FREECAD ASSEMBLY — COMPONENT RECIPES ("MotorFinAssembly")

This assembly document has 18 components, labeled P0..P17 below (a component is one placed body or linked part). 8 of them carry a construction recipe — the FreeCAD feature program that regenerates the part from scratch, quoted from this document or its linked companion documents; the rest are supplied as boundary geometry only. No exploded tour is included for this assembly.
COMPONENT P0 — geometry summary ("Mid Centering Ring"; no construction recipe available for this part):
  bounding box: 98.5 x 98.5 x 11.6 mm
  tessellated surface: 3,208 triangles
  volume: 51107 mm^3 (45% of its bounding box)
  symmetry: 2-fold rotationally symmetric about the x axis; 2-fold rotationally symmetric about the y axis; 4-fold rotationally symmetric about the z axis; mirror-symmetric across its x mid-plane, y mid-plane
COMPONENT P1 — geometry summary ("Fin001"; no construction recipe available for this part):
  bounding box: 304.8 x 108.1 x 108.1 mm
  tessellated surface: 44 triangles
  volume: 202568 mm^3 (6% of its bounding box)
COMPONENT P2 — geometry summary ("Fin002"; no construction recipe available for this part):
  bounding box: 304.8 x 108.1 x 108.1 mm
  tessellated surface: 44 triangles
  volume: 202568 mm^3 (6% of its bounding box)
COMPONENT P3 — geometry summary ("Fin003"; no construction recipe available for this part):
  bounding box: 304.8 x 108.1 x 108.1 mm
  tessellated surface: 44 triangles
  volume: 202568 mm^3 (6% of its bounding box)
COMPONENT P4 — geometry summary ("Fin004"; no construction recipe available for this part):
  bounding box: 304.8 x 108.1 x 108.1 mm
  tessellated surface: 44 triangles
  volume: 202568 mm^3 (6% of its bounding box)
COMPONENT P5 — geometry summary ("Aft Centering Ring"; no construction recipe available for this part):
  bounding box: 98.5 x 98.5 x 11.6 mm
  tessellated surface: 3,208 triangles
  volume: 51107 mm^3 (45% of its bounding box)
  symmetry: 2-fold rotationally symmetric about the x axis; 2-fold rotationally symmetric about the y axis; 4-fold rotationally symmetric about the z axis; mirror-symmetric across its x mid-plane, y mid-plane
COMPONENT P6 — geometry summary ("Motor Mount Tube"; no construction recipe available for this part):
  bounding box: 609.6 x 57.1 x 57.1 mm
  tessellated surface: 1,008 triangles
  volume: 167609 mm^3 (8% of its bounding box)
  symmetry: 2-fold rotationally symmetric about the x axis; 2-fold rotationally symmetric about the y axis; revolution-symmetric about the z axis through its bounding-box center; mirror-symmetric across its x mid-plane, y mid-plane, z mid-plane
COMPONENT P7 — geometry summary ("Thrust Plate"; no construction recipe available for this part):
  bounding box: 100.8 x 100.8 x 10.5 mm
  tessellated surface: 5,790 triangles
  volume: 53954 mm^3 (51% of its bounding box)
  symmetry: 3-fold rotationally symmetric about the z axis; mirror-symmetric across its x mid-plane
COMPONENT P8 — geometry summary ("Retainer Body"; no construction recipe available for this part):
  bounding box: 75.6 x 75.6 x 20.4 mm
  tessellated surface: 46,454 triangles
  volume: 12337 mm^3 (11% of its bounding box)
  symmetry: revolution-symmetric about the z axis through its bounding-box center; mirror-symmetric across its x mid-plane, y mid-plane
COMPONENT P9 — geometry summary ("Body"; no construction recipe available for this part):
  bounding box: 98.5 x 98.5 x 11.6 mm
  tessellated surface: 3,208 triangles
  volume: 51107 mm^3 (45% of its bounding box)
  symmetry: 2-fold rotationally symmetric about the x axis; 2-fold rotationally symmetric about the y axis; 4-fold rotationally symmetric about the z axis; mirror-symmetric across its x mid-plane, y mid-plane
COMPONENT P10 — recipe-attached ("90835A220_Dowel Nuts for Wood", a linked part whose construction recipe lives in a companion FreeCAD document of the same project; that document's serialized recipe follows).
Construction recipe (the companion document, serialized — sketch geometry with constraints, then the solid features built on it; lengths are millimeters unless a unit is written):

FCSTD DOCUMENT  (FreeCAD 1.0R39109 (Git))
Label: DowelNut
License: Creative Commons Attribution-ShareAlike 4.0
LicenseURL: https://creativecommons.org/licenses/by-sa/4.0/
objects: PartDesign::Body×1, Part::Feature×1
note: 2 computed .brp shape members not serialized (recipe doc carries the construction recipe); baked Part::Feature solids carry a one-line shape summary decoded from their .brp

FEATURE [PartDesign::Body] Body
  AllowCompound = false
  Origin = -> Origin
FEATURE [Part::Feature] Part__Feature  label="90835A220_Dowel Nuts for Wood"
  shape: bbox 12.7 x 9.982 x 11.97 mm, 60 faces (baked)
COMPONENT P11 — same part as P10; its construction recipe is shown at P10.
COMPONENT P12 — same part as P10; its construction recipe is shown at P10.
COMPONENT P13 — same part as P10; its construction recipe is shown at P10.
COMPONENT P14 — same part as P10; its construction recipe is shown at P10.
COMPONENT P15 — same part as P10; its construction recipe is shown at P10.
COMPONENT P16 — same part as P10; its construction recipe is shown at P10.
COMPONENT P17 — same part as P10; its construction recipe is shown at P10.
PROVENANCE & LICENSES
A FreeCAD (.FCStd) document from a public repository crawl; recipes are the document's own serialized feature recipes (and, for linked parts, companion documents' recipes).
License: mit.
